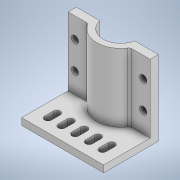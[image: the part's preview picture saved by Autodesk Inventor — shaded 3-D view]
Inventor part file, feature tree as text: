
AUTODESK INVENTOR PART (.ipt)
format: ipt  version: 2022 (Build 260153000, 153)  size: 202,752 bytes
history: native  units: in
note: dims shown in document units (in); Inventor stores cm internally (conversion verified against a paired STEP export)
features: sketch x4, extrude x3, hole x1, fillet x1
ambient origin geometry x8: Origin, YZ Plane, XZ Plane, XY Plane, X Axis, Y Axis, Z Axis, Center Point
bodies: Solid1 (feature_tree)
feature tree (9):
  extrude  "Extrusion1"  Depth=3.0in
  extrude  "Extrusion2"  Depth=0.25in
  hole  "Hole1"  [1 undecoded]
  fillet  "Fillet1"  Radius=1.75in
  extrude  "Extrusion3"  Depth=0.3in
  sketch  "Sketch1"  dims[d0=2.0in d1=3.0in]
  sketch  "Sketch2"  dims[d19=0.25in d20=0.0in d22=1.3in]
  sketch  "Sketch3"  dims[d23=0.125in d24=1.5in d25=1.75in]
  sketch  "Sketch6"  dims[d26=0.3in d27=0.3in d28=2.5in d29=0.0in d30=0.25in d31=0.25in d32=0.75in d33=0.75in d34=0.266in d35=0.75in d36=0.375in d37=0.25in d38=0.5635in d39=1.0in d40=0.8108in d41=0.325in d42=0.25in d43=0.5in d44=0.325in d45=0.25in d47=0.125in d49=1.3in d50=1.0in d51=0.0in d52=0.25in d53=0.25in d54=0.75in d55=0.75in d56=0.5in d57=0.625in d58=1.9685in d60=0.5in d61=0.3937in d63=1.0in]
note: 1 required parameter value undecoded (feature->parameter linkage not recoverable at this tier; creation-order binding heuristic only, values carry confidence <= 0.55)
